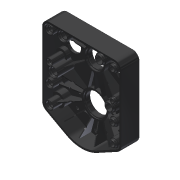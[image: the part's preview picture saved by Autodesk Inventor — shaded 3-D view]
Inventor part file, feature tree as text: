
AUTODESK INVENTOR PART (.ipt)
format: ipt  version: 2013 (Build 170138000, 138)  size: 775,680 bytes
history: native  units: in
note: dims shown in document units (in); Inventor stores cm internally (conversion verified against a paired STEP export)
features: fillet x1, other x1, imported_body x1
ambient origin geometry x8: Origin, YZ Plane, XZ Plane, XY Plane, X Axis, Y Axis, Z Axis, Center Point
feature tree (3):
  fillet  "Fillet18"  [1 undecoded]
  other  "217-2428-001 Rev11"
  imported_body  "Base1"
note: 1 required parameter value undecoded (feature->parameter linkage not recoverable at this tier; creation-order binding heuristic only, values carry confidence <= 0.55)
